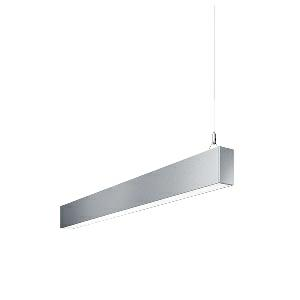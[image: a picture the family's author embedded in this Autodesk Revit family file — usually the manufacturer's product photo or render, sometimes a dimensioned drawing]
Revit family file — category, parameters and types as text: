
# Revit family: dotoo_line_-_dlp_1500_830_d_end_00805846_b7dd
name_source: partatom
category: Lighting Fixtures
units: mm (PartAtom-declared; Revit-internal decimal feet)

## family parameters
Cut with Voids When Loaded = No
Host = Face
Light Source = No
Part Type = Normal
Room Calculation Point = No
Round Connector Dimension = Use Diameter
Shared = No

## types (1)
- DOTOO.line - DLP 1500/830/D END (1 x LED, 1300 lm, 3000K)
    Apparent Load = 13 VA
    Approval mark = CE
    CIE Flux Codes = 67 91 98 100 100
    Color Rendering = 80-89
    Color Temperature = 3000K
    Control Gear = Electronic ballast
    Default Elevation = 1800 mm
    Description = DLP 1500/830/D|Suspended luminaire|light source: LED|connected load: 220-240 V, 50/60 Hz|Power consumption: approx. 13 W|standby: approx. 0,20|luminous flux: 1300 lm|luminous efficacy: 100 lm/W|light distribution: Direct|direct ratio: approx. 100 %|colour temperature: Warm white, ca. 3000 K|color rendering index (CRI): >= 80|chromaticity tolerance:  3 SDCM|System of protection: IP 40|technology: Continuously dimmable|luminaire body|material: Sectional aluminium|colour: Silver|lamp cover: Acrylic (PMMA), Clear|mains lead: 1,0 m With free stranded wires|Fastening: Steel cable 0.3 - 0.7 m|glare control: Prism aperture|luminance(L65): <= 3000 cd/m|unified glare rating(4H 8H): <=  19|special features: DALI Load 1x, TouchDIM - dimming via standard switch, Through-wired, up to 18 m on one mains connection, Flicker-free, Suitable as emergency lighting, Mechanical and electrical connection of the individual modules without tools|
    Frequency = 50 Hz
    Height = 110 mm
    Lamp = 1 x LED
    Lamp Light Flux = 1300 lm
    Lamp count = 1
    Length = 1128 mm
    Luminous efficacy = 100 lm/W
    Manufacturer = Waldmann
    ModVariant = No
    Model = 00805846
    Mounting Place = Ceiling
    Mounting Type = Pendant
    Number of Poles = 1
    OnlyDefault = Yes
    Power Factor = 1
    Product Name = DOTOO.line - DLP 1500/830/D END
    Product group = Suspended luminaire
    ProductGroupID = 9
    Protection Class = Protection class I
    Protection Degree = IP 40
    RLX_Detail_Level = 1
    RLX_Emergency_Light_Flux = 0 lm
    RLX_Emergency_Type = 0
    RLX_Emergency_Type_DB = No
    RlxData = <blob elided: 19985 chars, md5=44d63523>
    Socket = socket
    Standby Power = 0 W
    System Light Flux = 1300 lm
    System Power = 13 W
    Type Comments = Product without accessories
    Type Image = 113306000-00692582.jpg
    URL = http://relux.com
    VarID = ---
    Voltage = 230 V
    Voltage Range = 220-240 V
    Weight = 0.00 kg
    Width = 60 mm  [stored 0.19685 ft]

note: [stored X ft] marks values corroborated as IEEE doubles in the binary element streams (Revit-internal decimal feet)

## geometry (parser evidence)
native form markers: Blend x4, Sweep x12
no freeform markers — native parametric forms only
